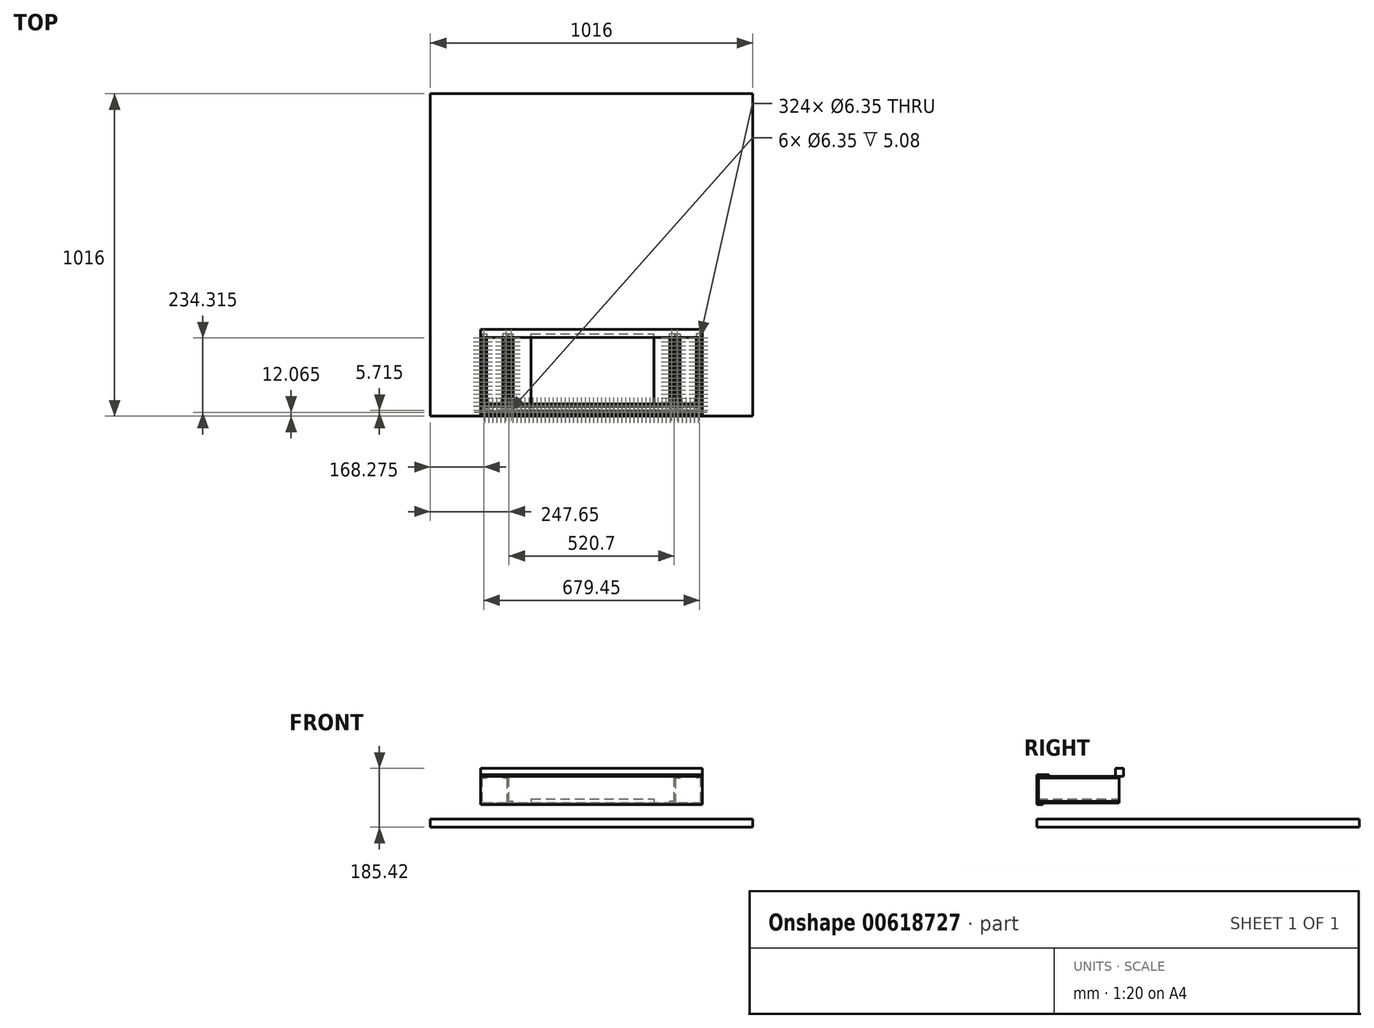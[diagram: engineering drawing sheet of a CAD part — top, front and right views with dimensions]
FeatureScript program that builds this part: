
annotation { "Feature Type Name" : "Feature", "Feature Type Description" : "" }
export const myFeature = defineFeature(function(context is Context, id is Id, definition is map)
    precondition{}
    {
        {
            var Q0;
            Q0=qCreatedBy(makeId("Top.planeOp"),FACE);
            var sketch = newSketch(context, id + "F0", { "sketchPlane" : qUnion([Q0])});
            skLineSegment(sketch, "E0.bottom", {"start": v(508, 508) * mm, "end": v(-508, 508) * mm});
            skLineSegment(sketch, "E0.top", {"start": v(508, -508) * mm, "end": v(-508, -508) * mm});
            skLineSegment(sketch, "E0.left", {"start": v(508, 508) * mm, "end": v(508, -508) * mm});
            skLineSegment(sketch, "E0.right", {"start": v(-508, 508) * mm, "end": v(-508, -508) * mm});
            skPoint(sketch, "E0.middle", {"position": v(0, 0) * mm});
            skSolve(sketch);
        }
        {
            var Q0;
            Q0 = qSketchRegion(id + "F0", true);
            extrude(context, id + "F1", {"entities" : qUnion([Q0]), "depth" : 25.4 * mm, "offsetDistance" : 25.4 * mm});
        }
        {
            var Q0;
            Q0=makeQuery(id+"F1.opExtrude","SWEPT_FACE",FACE,{"disambiguationData":[OSD([sQuery(id+"F0.wireOp",EDGE,"E0.top")])]});
            var sketch = newSketch(context, id + "F2", { "sketchPlane" : qUnion([Q0])});
            skLineSegment(sketch, "E1.bottom", {"start": v(-349.25, 165.1) * mm, "end": v(349.25, 165.1) * mm});
            skLineSegment(sketch, "E1.top", {"start": v(-349.25, 76.2) * mm, "end": v(349.25, 76.2) * mm});
            skLineSegment(sketch, "E1.left", {"start": v(-349.25, 165.1) * mm, "end": v(-349.25, 76.2) * mm});
            skLineSegment(sketch, "E1.right", {"start": v(349.25, 165.1) * mm, "end": v(349.25, 76.2) * mm});
            skSolve(sketch);
        }
        {
            var Q0;
            Q0 = qSketchRegion(id + "F2", true);
            extrude(context, id + "F3", {"entities" : qUnion([Q0]), "oppositeDirection" : true, "depth" : 5.08 * mm, "offsetDistance" : 25.4 * mm});
        }
        {
            var Q0;
            Q0=makeQuery(id+"F3.opExtrude","SWEPT_FACE",FACE,{"disambiguationData":[OSD([sQuery(id+"F2.wireOp",EDGE,"E1.bottom")])]});
            var sketch = newSketch(context, id + "F4", { "sketchPlane" : qUnion([Q0])});
            skLineSegment(sketch, "E2.bottom", {"start": v(-349.25, -469.9) * mm, "end": v(349.25, -469.9) * mm});
            skLineSegment(sketch, "E2.top", {"start": v(-349.25, -508) * mm, "end": v(349.25, -508) * mm});
            skLineSegment(sketch, "E2.left", {"start": v(-349.25, -469.9) * mm, "end": v(-349.25, -508) * mm});
            skLineSegment(sketch, "E2.right", {"start": v(349.25, -469.9) * mm, "end": v(349.25, -508) * mm});
            skCircle(sketch, "E3", {"center": v(-336.55, -476.25) * mm, "radius": 3.18 * mm});
            skCircle(sketch, "E4.0.1.0", {"center": v(-335.43, -495.27) * mm, "radius": 3.18 * mm});
            skCircle(sketch, "E4.1.0.0", {"center": v(-323.85, -476.25) * mm, "radius": 3.18 * mm});
            skCircle(sketch, "E4.1.1.0", {"center": v(-322.73, -495.27) * mm, "radius": 3.18 * mm});
            skCircle(sketch, "E4.2.0.0", {"center": v(-311.15, -476.25) * mm, "radius": 3.18 * mm});
            skCircle(sketch, "E4.2.1.0", {"center": v(-310.03, -495.27) * mm, "radius": 3.18 * mm});
            skCircle(sketch, "E4.3.0.0", {"center": v(-298.45, -476.25) * mm, "radius": 3.18 * mm});
            skCircle(sketch, "E4.3.1.0", {"center": v(-297.33, -495.27) * mm, "radius": 3.18 * mm});
            skCircle(sketch, "E4.4.0.0", {"center": v(-285.75, -476.25) * mm, "radius": 3.18 * mm});
            skCircle(sketch, "E4.4.1.0", {"center": v(-284.63, -495.27) * mm, "radius": 3.18 * mm});
            skCircle(sketch, "E4.5.0.0", {"center": v(-273.05, -476.25) * mm, "radius": 3.18 * mm});
            skCircle(sketch, "E4.5.1.0", {"center": v(-271.93, -495.27) * mm, "radius": 3.18 * mm});
            skCircle(sketch, "E4.6.0.0", {"center": v(-260.35, -476.25) * mm, "radius": 3.18 * mm});
            skCircle(sketch, "E4.6.1.0", {"center": v(-259.23, -495.27) * mm, "radius": 3.18 * mm});
            skCircle(sketch, "E4.7.0.0", {"center": v(-247.65, -476.25) * mm, "radius": 3.18 * mm});
            skCircle(sketch, "E4.7.1.0", {"center": v(-246.53, -495.27) * mm, "radius": 3.18 * mm});
            skCircle(sketch, "E4.8.0.0", {"center": v(-234.95, -476.25) * mm, "radius": 3.18 * mm});
            skCircle(sketch, "E4.8.1.0", {"center": v(-233.83, -495.27) * mm, "radius": 3.18 * mm});
            skCircle(sketch, "E4.9.0.0", {"center": v(-222.25, -476.25) * mm, "radius": 3.18 * mm});
            skCircle(sketch, "E4.9.1.0", {"center": v(-221.13, -495.27) * mm, "radius": 3.18 * mm});
            skCircle(sketch, "E4.10.0.0", {"center": v(-209.55, -476.25) * mm, "radius": 3.18 * mm});
            skCircle(sketch, "E4.10.1.0", {"center": v(-208.43, -495.27) * mm, "radius": 3.18 * mm});
            skCircle(sketch, "E4.11.0.0", {"center": v(-196.85, -476.25) * mm, "radius": 3.18 * mm});
            skCircle(sketch, "E4.11.1.0", {"center": v(-195.73, -495.27) * mm, "radius": 3.18 * mm});
            skCircle(sketch, "E4.12.0.0", {"center": v(-184.15, -476.25) * mm, "radius": 3.18 * mm});
            skCircle(sketch, "E4.12.1.0", {"center": v(-183.03, -495.27) * mm, "radius": 3.18 * mm});
            skCircle(sketch, "E4.13.0.0", {"center": v(-171.45, -476.25) * mm, "radius": 3.18 * mm});
            skCircle(sketch, "E4.13.1.0", {"center": v(-170.33, -495.27) * mm, "radius": 3.18 * mm});
            skCircle(sketch, "E4.14.0.0", {"center": v(-158.75, -476.25) * mm, "radius": 3.18 * mm});
            skCircle(sketch, "E4.14.1.0", {"center": v(-157.63, -495.27) * mm, "radius": 3.18 * mm});
            skCircle(sketch, "E4.15.0.0", {"center": v(-146.05, -476.25) * mm, "radius": 3.18 * mm});
            skCircle(sketch, "E4.15.1.0", {"center": v(-144.93, -495.27) * mm, "radius": 3.18 * mm});
            skCircle(sketch, "E4.16.0.0", {"center": v(-133.35, -476.25) * mm, "radius": 3.18 * mm});
            skCircle(sketch, "E4.16.1.0", {"center": v(-132.23, -495.27) * mm, "radius": 3.18 * mm});
            skCircle(sketch, "E4.17.0.0", {"center": v(-120.65, -476.25) * mm, "radius": 3.18 * mm});
            skCircle(sketch, "E4.17.1.0", {"center": v(-119.53, -495.27) * mm, "radius": 3.18 * mm});
            skCircle(sketch, "E4.18.0.0", {"center": v(-107.95, -476.25) * mm, "radius": 3.18 * mm});
            skCircle(sketch, "E4.18.1.0", {"center": v(-106.83, -495.27) * mm, "radius": 3.18 * mm});
            skCircle(sketch, "E4.19.0.0", {"center": v(-95.25, -476.25) * mm, "radius": 3.18 * mm});
            skCircle(sketch, "E4.19.1.0", {"center": v(-94.13, -495.27) * mm, "radius": 3.18 * mm});
            skCircle(sketch, "E4.20.0.0", {"center": v(-82.55, -476.25) * mm, "radius": 3.18 * mm});
            skCircle(sketch, "E4.20.1.0", {"center": v(-81.43, -495.27) * mm, "radius": 3.18 * mm});
            skCircle(sketch, "E4.21.0.0", {"center": v(-69.85, -476.25) * mm, "radius": 3.18 * mm});
            skCircle(sketch, "E4.21.1.0", {"center": v(-68.73, -495.27) * mm, "radius": 3.18 * mm});
            skCircle(sketch, "E4.22.0.0", {"center": v(-57.15, -476.25) * mm, "radius": 3.18 * mm});
            skCircle(sketch, "E4.22.1.0", {"center": v(-56.03, -495.27) * mm, "radius": 3.18 * mm});
            skCircle(sketch, "E4.23.0.0", {"center": v(-44.45, -476.25) * mm, "radius": 3.18 * mm});
            skCircle(sketch, "E4.23.1.0", {"center": v(-43.33, -495.27) * mm, "radius": 3.18 * mm});
            skCircle(sketch, "E4.24.0.0", {"center": v(-31.75, -476.25) * mm, "radius": 3.18 * mm});
            skCircle(sketch, "E4.24.1.0", {"center": v(-30.63, -495.27) * mm, "radius": 3.18 * mm});
            skCircle(sketch, "E4.25.0.0", {"center": v(-19.05, -476.25) * mm, "radius": 3.18 * mm});
            skCircle(sketch, "E4.25.1.0", {"center": v(-17.93, -495.27) * mm, "radius": 3.18 * mm});
            skCircle(sketch, "E4.26.0.0", {"center": v(-6.35, -476.25) * mm, "radius": 3.18 * mm});
            skCircle(sketch, "E4.26.1.0", {"center": v(-5.23, -495.27) * mm, "radius": 3.18 * mm});
            skCircle(sketch, "E4.27.0.0", {"center": v(6.35, -476.25) * mm, "radius": 3.18 * mm});
            skCircle(sketch, "E4.27.1.0", {"center": v(7.47, -495.27) * mm, "radius": 3.18 * mm});
            skCircle(sketch, "E4.28.0.0", {"center": v(19.05, -476.25) * mm, "radius": 3.18 * mm});
            skCircle(sketch, "E4.28.1.0", {"center": v(20.17, -495.27) * mm, "radius": 3.18 * mm});
            skCircle(sketch, "E4.29.0.0", {"center": v(31.75, -476.25) * mm, "radius": 3.18 * mm});
            skCircle(sketch, "E4.29.1.0", {"center": v(32.87, -495.27) * mm, "radius": 3.18 * mm});
            skCircle(sketch, "E4.30.0.0", {"center": v(44.45, -476.25) * mm, "radius": 3.18 * mm});
            skCircle(sketch, "E4.30.1.0", {"center": v(45.57, -495.27) * mm, "radius": 3.18 * mm});
            skCircle(sketch, "E4.31.0.0", {"center": v(57.15, -476.25) * mm, "radius": 3.18 * mm});
            skCircle(sketch, "E4.31.1.0", {"center": v(58.27, -495.27) * mm, "radius": 3.18 * mm});
            skCircle(sketch, "E4.32.0.0", {"center": v(69.85, -476.25) * mm, "radius": 3.18 * mm});
            skCircle(sketch, "E4.32.1.0", {"center": v(70.97, -495.27) * mm, "radius": 3.18 * mm});
            skCircle(sketch, "E4.33.0.0", {"center": v(82.55, -476.25) * mm, "radius": 3.18 * mm});
            skCircle(sketch, "E4.33.1.0", {"center": v(83.67, -495.27) * mm, "radius": 3.18 * mm});
            skCircle(sketch, "E4.34.0.0", {"center": v(95.25, -476.25) * mm, "radius": 3.18 * mm});
            skCircle(sketch, "E4.34.1.0", {"center": v(96.37, -495.27) * mm, "radius": 3.18 * mm});
            skCircle(sketch, "E4.35.0.0", {"center": v(107.95, -476.25) * mm, "radius": 3.18 * mm});
            skCircle(sketch, "E4.35.1.0", {"center": v(109.07, -495.27) * mm, "radius": 3.18 * mm});
            skCircle(sketch, "E4.36.0.0", {"center": v(120.65, -476.25) * mm, "radius": 3.18 * mm});
            skCircle(sketch, "E4.36.1.0", {"center": v(121.77, -495.27) * mm, "radius": 3.18 * mm});
            skCircle(sketch, "E4.37.0.0", {"center": v(133.35, -476.25) * mm, "radius": 3.18 * mm});
            skCircle(sketch, "E4.37.1.0", {"center": v(134.47, -495.27) * mm, "radius": 3.18 * mm});
            skCircle(sketch, "E4.38.0.0", {"center": v(146.05, -476.25) * mm, "radius": 3.18 * mm});
            skCircle(sketch, "E4.38.1.0", {"center": v(147.17, -495.27) * mm, "radius": 3.18 * mm});
            skCircle(sketch, "E4.39.0.0", {"center": v(158.75, -476.25) * mm, "radius": 3.18 * mm});
            skCircle(sketch, "E4.39.1.0", {"center": v(159.87, -495.27) * mm, "radius": 3.18 * mm});
            skCircle(sketch, "E4.40.0.0", {"center": v(171.45, -476.25) * mm, "radius": 3.18 * mm});
            skCircle(sketch, "E4.40.1.0", {"center": v(172.57, -495.27) * mm, "radius": 3.18 * mm});
            skCircle(sketch, "E4.41.0.0", {"center": v(184.15, -476.25) * mm, "radius": 3.18 * mm});
            skCircle(sketch, "E4.41.1.0", {"center": v(185.27, -495.27) * mm, "radius": 3.18 * mm});
            skCircle(sketch, "E4.42.0.0", {"center": v(196.85, -476.25) * mm, "radius": 3.18 * mm});
            skCircle(sketch, "E4.42.1.0", {"center": v(197.97, -495.27) * mm, "radius": 3.18 * mm});
            skCircle(sketch, "E4.43.0.0", {"center": v(209.55, -476.25) * mm, "radius": 3.18 * mm});
            skCircle(sketch, "E4.43.1.0", {"center": v(210.67, -495.27) * mm, "radius": 3.18 * mm});
            skCircle(sketch, "E4.44.0.0", {"center": v(222.25, -476.25) * mm, "radius": 3.18 * mm});
            skCircle(sketch, "E4.44.1.0", {"center": v(223.37, -495.27) * mm, "radius": 3.18 * mm});
            skCircle(sketch, "E4.45.0.0", {"center": v(234.95, -476.25) * mm, "radius": 3.18 * mm});
            skCircle(sketch, "E4.45.1.0", {"center": v(236.07, -495.27) * mm, "radius": 3.18 * mm});
            skCircle(sketch, "E4.46.0.0", {"center": v(247.65, -476.25) * mm, "radius": 3.18 * mm});
            skCircle(sketch, "E4.46.1.0", {"center": v(248.77, -495.27) * mm, "radius": 3.18 * mm});
            skCircle(sketch, "E4.47.0.0", {"center": v(260.35, -476.25) * mm, "radius": 3.18 * mm});
            skCircle(sketch, "E4.47.1.0", {"center": v(261.47, -495.27) * mm, "radius": 3.18 * mm});
            skCircle(sketch, "E4.48.0.0", {"center": v(273.05, -476.25) * mm, "radius": 3.18 * mm});
            skCircle(sketch, "E4.48.1.0", {"center": v(274.17, -495.27) * mm, "radius": 3.18 * mm});
            skCircle(sketch, "E4.49.0.0", {"center": v(285.75, -476.25) * mm, "radius": 3.18 * mm});
            skCircle(sketch, "E4.49.1.0", {"center": v(286.87, -495.27) * mm, "radius": 3.18 * mm});
            skCircle(sketch, "E4.50.0.0", {"center": v(298.45, -476.25) * mm, "radius": 3.18 * mm});
            skCircle(sketch, "E4.50.1.0", {"center": v(299.57, -495.27) * mm, "radius": 3.18 * mm});
            skCircle(sketch, "E4.51.0.0", {"center": v(311.15, -476.25) * mm, "radius": 3.18 * mm});
            skCircle(sketch, "E4.51.1.0", {"center": v(312.27, -495.27) * mm, "radius": 3.18 * mm});
            skCircle(sketch, "E4.52.0.0", {"center": v(323.85, -476.25) * mm, "radius": 3.18 * mm});
            skCircle(sketch, "E4.52.1.0", {"center": v(324.97, -495.27) * mm, "radius": 3.18 * mm});
            skCircle(sketch, "E4.53.0.0", {"center": v(336.55, -476.25) * mm, "radius": 3.18 * mm});
            skCircle(sketch, "E4.53.1.0", {"center": v(337.67, -495.27) * mm, "radius": 3.18 * mm});
            skLineSegment(sketch, "E4.direction1", {"start": v(-336.55, -476.25) * mm, "end": v(-323.85, -476.25) * mm, "construction": true});
            skLineSegment(sketch, "E4.direction2", {"start": v(-336.55, -476.25) * mm, "end": v(-335.43, -495.27) * mm, "construction": true});
            skSolve(sketch);
        }
        {
            var Q0;
            Q0 = qSketchRegion(id + "F4", true);
            extrude(context, id + "F5", {"entities" : qUnion([Q0]), "oppositeDirection" : true, "depth" : 5.08 * mm, "offsetDistance" : 25.4 * mm});
        }
        {
            var Q0;
            Q0=makeQuery(id+"F3.opExtrude","SWEPT_FACE",FACE,{"disambiguationData":[OSD([sQuery(id+"F2.wireOp",EDGE,"E1.top")])]});
            var sketch = newSketch(context, id + "F6", { "sketchPlane" : qUnion([Q0])});
            skLineSegment(sketch, "E5.bottom", {"start": v(-349.25, 508) * mm, "end": v(349.25, 508) * mm});
            skLineSegment(sketch, "E5.top", {"start": v(-349.25, 488.95) * mm, "end": v(349.25, 488.95) * mm});
            skLineSegment(sketch, "E5.left", {"start": v(-349.25, 508) * mm, "end": v(-349.25, 488.95) * mm});
            skLineSegment(sketch, "E5.right", {"start": v(349.25, 508) * mm, "end": v(349.25, 488.95) * mm});
            skCircle(sketch, "E6", {"center": v(-336.55, 495.94) * mm, "radius": 3.18 * mm});
            skCircle(sketch, "E7.1.0.0", {"center": v(-323.85, 495.94) * mm, "radius": 3.18 * mm});
            skCircle(sketch, "E7.2.0.0", {"center": v(-311.15, 495.94) * mm, "radius": 3.18 * mm});
            skCircle(sketch, "E7.3.0.0", {"center": v(-298.45, 495.94) * mm, "radius": 3.18 * mm});
            skCircle(sketch, "E7.4.0.0", {"center": v(-285.75, 495.94) * mm, "radius": 3.18 * mm});
            skCircle(sketch, "E7.5.0.0", {"center": v(-273.05, 495.94) * mm, "radius": 3.18 * mm});
            skCircle(sketch, "E7.6.0.0", {"center": v(-260.35, 495.94) * mm, "radius": 3.18 * mm});
            skCircle(sketch, "E7.7.0.0", {"center": v(-247.65, 495.94) * mm, "radius": 3.18 * mm});
            skCircle(sketch, "E7.8.0.0", {"center": v(-234.95, 495.94) * mm, "radius": 3.18 * mm});
            skCircle(sketch, "E7.9.0.0", {"center": v(-222.25, 495.94) * mm, "radius": 3.18 * mm});
            skCircle(sketch, "E7.10.0.0", {"center": v(-209.55, 495.94) * mm, "radius": 3.18 * mm});
            skCircle(sketch, "E7.11.0.0", {"center": v(-196.85, 495.94) * mm, "radius": 3.18 * mm});
            skCircle(sketch, "E7.12.0.0", {"center": v(-184.15, 495.94) * mm, "radius": 3.18 * mm});
            skCircle(sketch, "E7.13.0.0", {"center": v(-171.45, 495.94) * mm, "radius": 3.18 * mm});
            skCircle(sketch, "E7.14.0.0", {"center": v(-158.75, 495.94) * mm, "radius": 3.18 * mm});
            skCircle(sketch, "E7.15.0.0", {"center": v(-146.05, 495.94) * mm, "radius": 3.18 * mm});
            skCircle(sketch, "E7.16.0.0", {"center": v(-133.35, 495.94) * mm, "radius": 3.18 * mm});
            skCircle(sketch, "E7.17.0.0", {"center": v(-120.65, 495.94) * mm, "radius": 3.18 * mm});
            skCircle(sketch, "E7.18.0.0", {"center": v(-107.95, 495.94) * mm, "radius": 3.18 * mm});
            skCircle(sketch, "E7.19.0.0", {"center": v(-95.25, 495.94) * mm, "radius": 3.18 * mm});
            skCircle(sketch, "E7.20.0.0", {"center": v(-82.55, 495.94) * mm, "radius": 3.18 * mm});
            skCircle(sketch, "E7.21.0.0", {"center": v(-69.85, 495.94) * mm, "radius": 3.18 * mm});
            skCircle(sketch, "E7.22.0.0", {"center": v(-57.15, 495.94) * mm, "radius": 3.18 * mm});
            skCircle(sketch, "E7.23.0.0", {"center": v(-44.45, 495.94) * mm, "radius": 3.18 * mm});
            skCircle(sketch, "E7.24.0.0", {"center": v(-31.75, 495.94) * mm, "radius": 3.18 * mm});
            skCircle(sketch, "E7.25.0.0", {"center": v(-19.05, 495.94) * mm, "radius": 3.18 * mm});
            skCircle(sketch, "E7.26.0.0", {"center": v(-6.35, 495.94) * mm, "radius": 3.18 * mm});
            skCircle(sketch, "E7.27.0.0", {"center": v(6.35, 495.94) * mm, "radius": 3.18 * mm});
            skCircle(sketch, "E7.28.0.0", {"center": v(19.05, 495.94) * mm, "radius": 3.18 * mm});
            skCircle(sketch, "E7.29.0.0", {"center": v(31.75, 495.94) * mm, "radius": 3.18 * mm});
            skCircle(sketch, "E7.30.0.0", {"center": v(44.45, 495.94) * mm, "radius": 3.18 * mm});
            skCircle(sketch, "E7.31.0.0", {"center": v(57.15, 495.94) * mm, "radius": 3.18 * mm});
            skCircle(sketch, "E7.32.0.0", {"center": v(69.85, 495.94) * mm, "radius": 3.18 * mm});
            skCircle(sketch, "E7.33.0.0", {"center": v(82.55, 495.94) * mm, "radius": 3.18 * mm});
            skCircle(sketch, "E7.34.0.0", {"center": v(95.25, 495.94) * mm, "radius": 3.18 * mm});
            skCircle(sketch, "E7.35.0.0", {"center": v(107.95, 495.94) * mm, "radius": 3.18 * mm});
            skCircle(sketch, "E7.36.0.0", {"center": v(120.65, 495.94) * mm, "radius": 3.18 * mm});
            skCircle(sketch, "E7.37.0.0", {"center": v(133.35, 495.94) * mm, "radius": 3.18 * mm});
            skCircle(sketch, "E7.38.0.0", {"center": v(146.05, 495.94) * mm, "radius": 3.18 * mm});
            skCircle(sketch, "E7.39.0.0", {"center": v(158.75, 495.94) * mm, "radius": 3.18 * mm});
            skCircle(sketch, "E7.40.0.0", {"center": v(171.45, 495.94) * mm, "radius": 3.18 * mm});
            skCircle(sketch, "E7.41.0.0", {"center": v(184.15, 495.94) * mm, "radius": 3.18 * mm});
            skCircle(sketch, "E7.42.0.0", {"center": v(196.85, 495.94) * mm, "radius": 3.18 * mm});
            skCircle(sketch, "E7.43.0.0", {"center": v(209.55, 495.94) * mm, "radius": 3.18 * mm});
            skCircle(sketch, "E7.44.0.0", {"center": v(222.25, 495.94) * mm, "radius": 3.18 * mm});
            skCircle(sketch, "E7.45.0.0", {"center": v(234.95, 495.94) * mm, "radius": 3.18 * mm});
            skCircle(sketch, "E7.46.0.0", {"center": v(247.65, 495.94) * mm, "radius": 3.18 * mm});
            skCircle(sketch, "E7.47.0.0", {"center": v(260.35, 495.94) * mm, "radius": 3.18 * mm});
            skCircle(sketch, "E7.48.0.0", {"center": v(273.05, 495.94) * mm, "radius": 3.18 * mm});
            skCircle(sketch, "E7.49.0.0", {"center": v(285.75, 495.94) * mm, "radius": 3.18 * mm});
            skCircle(sketch, "E7.50.0.0", {"center": v(298.45, 495.94) * mm, "radius": 3.18 * mm});
            skCircle(sketch, "E7.51.0.0", {"center": v(311.15, 495.94) * mm, "radius": 3.18 * mm});
            skCircle(sketch, "E7.52.0.0", {"center": v(323.85, 495.94) * mm, "radius": 3.18 * mm});
            skCircle(sketch, "E7.53.0.0", {"center": v(336.55, 495.94) * mm, "radius": 3.18 * mm});
            skLineSegment(sketch, "E7.direction1", {"start": v(-336.55, 495.94) * mm, "end": v(-323.85, 495.94) * mm, "construction": true});
            skSolve(sketch);
        }
        {
            var Q0;
            Q0 = qSketchRegion(id + "F6", true);
            extrude(context, id + "F7", {"entities" : qUnion([Q0]), "operationType" : NewBodyOperationType.ADD, "depth" : 5.08 * mm, "offsetDistance" : 25.4 * mm});
        }
        {
            var Q0;
            Q0=makeQuery(id+"F3.opExtrude","CAP_FACE",FACE,{"disambiguationData":[OSD([sQuery(id+"F2.wireOp",EDGE,"E1.bottom"),sQuery(id+"F2.wireOp",EDGE,"E1.top"),sQuery(id+"F2.wireOp",EDGE,"E1.left"),sQuery(id+"F2.wireOp",EDGE,"E1.right")])],"isStart":false});
            var sketch = newSketch(context, id + "F8", { "sketchPlane" : qUnion([Q0])});
            skLineSegment(sketch, "E8.top", {"start": v(-349.25, 154.94) * mm, "end": v(-344.17, 154.94) * mm});
            skLineSegment(sketch, "E8.left", {"start": v(-349.25, 81.28) * mm, "end": v(-349.25, 154.94) * mm});
            skLineSegment(sketch, "E8.right", {"start": v(-344.17, 81.28) * mm, "end": v(-344.17, 154.94) * mm});
            skLineSegment(sketch, "E9.top", {"start": v(-265.43, 154.94) * mm, "end": v(-260.35, 154.94) * mm});
            skLineSegment(sketch, "E9.left", {"start": v(-265.43, 81.28) * mm, "end": v(-265.43, 154.94) * mm});
            skLineSegment(sketch, "E9.right", {"start": v(-260.35, 81.28) * mm, "end": v(-260.35, 154.94) * mm});
            skLineSegment(sketch, "E10", {"start": v(-265.43, 81.28) * mm, "end": v(-260.35, 81.28) * mm});
            skLineSegment(sketch, "E11", {"start": v(-349.25, 81.28) * mm, "end": v(-344.17, 81.28) * mm});
            skSolve(sketch);
        }
        {
            var Q0;
            Q0 = qSketchRegion(id + "F8", true);
            extrude(context, id + "F9", {"entities" : qUnion([Q0]), "operationType" : NewBodyOperationType.ADD, "depth" : 254 * mm, "offsetDistance" : 25.4 * mm});
        }
        {
            var Q0;
            Q0=makeQuery(id+"F9.opExtrude","SWEPT_FACE",FACE,{"disambiguationData":[OSD([sQuery(id+"F8.wireOp",EDGE,"E8.top")])]});
            var sketch = newSketch(context, id + "F10", { "sketchPlane" : qUnion([Q0])});
            skLineSegment(sketch, "E12.bottom", {"start": v(349.25, -248.92) * mm, "end": v(330.2, -248.92) * mm});
            skLineSegment(sketch, "E12.top", {"start": v(349.25, -502.92) * mm, "end": v(330.2, -502.92) * mm});
            skLineSegment(sketch, "E12.left", {"start": v(349.25, -248.92) * mm, "end": v(349.25, -502.92) * mm});
            skLineSegment(sketch, "E12.right", {"start": v(330.2, -248.92) * mm, "end": v(330.2, -502.92) * mm});
            skLineSegment(sketch, "E13.bottom", {"start": v(260.35, -248.92) * mm, "end": v(279.4, -248.92) * mm});
            skLineSegment(sketch, "E13.top", {"start": v(260.35, -502.92) * mm, "end": v(279.4, -502.92) * mm});
            skLineSegment(sketch, "E13.left", {"start": v(260.35, -248.92) * mm, "end": v(260.35, -502.92) * mm});
            skLineSegment(sketch, "E13.right", {"start": v(279.4, -248.92) * mm, "end": v(279.4, -502.92) * mm});
            skCircle(sketch, "E14", {"center": v(269.88, -261.62) * mm, "radius": 3.18 * mm});
            skCircle(sketch, "E15.0.1.0", {"center": v(269.88, -274.32) * mm, "radius": 3.18 * mm});
            skCircle(sketch, "E15.0.2.0", {"center": v(269.88, -287.02) * mm, "radius": 3.18 * mm});
            skCircle(sketch, "E15.0.3.0", {"center": v(269.88, -299.72) * mm, "radius": 3.18 * mm});
            skCircle(sketch, "E15.0.4.0", {"center": v(269.88, -312.42) * mm, "radius": 3.18 * mm});
            skCircle(sketch, "E15.0.5.0", {"center": v(269.88, -325.12) * mm, "radius": 3.18 * mm});
            skCircle(sketch, "E15.0.6.0", {"center": v(269.88, -337.82) * mm, "radius": 3.18 * mm});
            skCircle(sketch, "E15.0.7.0", {"center": v(269.88, -350.52) * mm, "radius": 3.18 * mm});
            skCircle(sketch, "E15.0.8.0", {"center": v(269.88, -363.22) * mm, "radius": 3.18 * mm});
            skCircle(sketch, "E15.0.9.0", {"center": v(269.88, -375.92) * mm, "radius": 3.18 * mm});
            skCircle(sketch, "E15.0.10.0", {"center": v(269.88, -388.62) * mm, "radius": 3.18 * mm});
            skCircle(sketch, "E15.0.11.0", {"center": v(269.88, -401.32) * mm, "radius": 3.18 * mm});
            skCircle(sketch, "E15.0.12.0", {"center": v(269.88, -414.02) * mm, "radius": 3.18 * mm});
            skCircle(sketch, "E15.0.13.0", {"center": v(269.88, -426.72) * mm, "radius": 3.18 * mm});
            skCircle(sketch, "E15.0.14.0", {"center": v(269.88, -439.42) * mm, "radius": 3.18 * mm});
            skCircle(sketch, "E15.0.15.0", {"center": v(269.88, -452.12) * mm, "radius": 3.18 * mm});
            skCircle(sketch, "E15.0.16.0", {"center": v(269.88, -464.82) * mm, "radius": 3.18 * mm});
            skCircle(sketch, "E15.0.17.0", {"center": v(269.88, -477.52) * mm, "radius": 3.18 * mm});
            skCircle(sketch, "E15.0.18.0", {"center": v(269.88, -490.22) * mm, "radius": 3.18 * mm});
            skCircle(sketch, "E15.1.0.0", {"center": v(339.73, -261.62) * mm, "radius": 3.18 * mm});
            skCircle(sketch, "E15.1.1.0", {"center": v(339.73, -274.32) * mm, "radius": 3.18 * mm});
            skCircle(sketch, "E15.1.2.0", {"center": v(339.73, -287.02) * mm, "radius": 3.18 * mm});
            skCircle(sketch, "E15.1.3.0", {"center": v(339.73, -299.72) * mm, "radius": 3.18 * mm});
            skCircle(sketch, "E15.1.4.0", {"center": v(339.73, -312.42) * mm, "radius": 3.18 * mm});
            skCircle(sketch, "E15.1.5.0", {"center": v(339.73, -325.12) * mm, "radius": 3.18 * mm});
            skCircle(sketch, "E15.1.6.0", {"center": v(339.73, -337.82) * mm, "radius": 3.18 * mm});
            skCircle(sketch, "E15.1.7.0", {"center": v(339.73, -350.52) * mm, "radius": 3.18 * mm});
            skCircle(sketch, "E15.1.8.0", {"center": v(339.73, -363.22) * mm, "radius": 3.18 * mm});
            skCircle(sketch, "E15.1.9.0", {"center": v(339.73, -375.92) * mm, "radius": 3.18 * mm});
            skCircle(sketch, "E15.1.10.0", {"center": v(339.73, -388.62) * mm, "radius": 3.18 * mm});
            skCircle(sketch, "E15.1.11.0", {"center": v(339.73, -401.32) * mm, "radius": 3.18 * mm});
            skCircle(sketch, "E15.1.12.0", {"center": v(339.73, -414.02) * mm, "radius": 3.18 * mm});
            skCircle(sketch, "E15.1.13.0", {"center": v(339.73, -426.72) * mm, "radius": 3.18 * mm});
            skCircle(sketch, "E15.1.14.0", {"center": v(339.73, -439.42) * mm, "radius": 3.18 * mm});
            skCircle(sketch, "E15.1.15.0", {"center": v(339.73, -452.12) * mm, "radius": 3.18 * mm});
            skCircle(sketch, "E15.1.16.0", {"center": v(339.73, -464.82) * mm, "radius": 3.18 * mm});
            skCircle(sketch, "E15.1.17.0", {"center": v(339.73, -477.52) * mm, "radius": 3.18 * mm});
            skCircle(sketch, "E15.1.18.0", {"center": v(339.73, -490.22) * mm, "radius": 3.18 * mm});
            skLineSegment(sketch, "E15.direction1", {"start": v(269.88, -261.62) * mm, "end": v(339.73, -261.62) * mm, "construction": true});
            skLineSegment(sketch, "E15.direction2", {"start": v(269.88, -261.62) * mm, "end": v(269.88, -274.32) * mm, "construction": true});
            skSolve(sketch);
        }
        {
            var Q0;
            Q0 = qSketchRegion(id + "F10", true);
            extrude(context, id + "F11", {"entities" : qUnion([Q0]), "depth" : 5.08 * mm, "offsetDistance" : 25.4 * mm});
        }
        {
            var Q0;
            Q0=makeQuery(id+"F9.opExtrude","SWEPT_FACE",FACE,{"disambiguationData":[OSD([sQuery(id+"F8.wireOp",EDGE,"E10")])]});
            var sketch = newSketch(context, id + "F12", { "sketchPlane" : qUnion([Q0])});
            skLineSegment(sketch, "E16.bottom", {"start": v(246.38, 502.92) * mm, "end": v(265.43, 502.92) * mm});
            skLineSegment(sketch, "E16.top", {"start": v(246.38, 248.92) * mm, "end": v(265.43, 248.92) * mm});
            skLineSegment(sketch, "E16.left", {"start": v(246.38, 502.92) * mm, "end": v(246.38, 248.92) * mm});
            skLineSegment(sketch, "E16.right", {"start": v(265.43, 502.92) * mm, "end": v(265.43, 248.92) * mm});
            skCircle(sketch, "E17", {"center": v(252.73, 261.62) * mm, "radius": 3.18 * mm});
            skCircle(sketch, "E18.0.1.0", {"center": v(252.73, 274.32) * mm, "radius": 3.18 * mm});
            skCircle(sketch, "E18.0.2.0", {"center": v(252.73, 287.02) * mm, "radius": 3.18 * mm});
            skCircle(sketch, "E18.0.3.0", {"center": v(252.73, 299.72) * mm, "radius": 3.18 * mm});
            skCircle(sketch, "E18.0.4.0", {"center": v(252.73, 312.42) * mm, "radius": 3.18 * mm});
            skCircle(sketch, "E18.0.5.0", {"center": v(252.73, 325.12) * mm, "radius": 3.18 * mm});
            skCircle(sketch, "E18.0.6.0", {"center": v(252.73, 337.82) * mm, "radius": 3.18 * mm});
            skCircle(sketch, "E18.0.7.0", {"center": v(252.73, 350.52) * mm, "radius": 3.18 * mm});
            skCircle(sketch, "E18.0.8.0", {"center": v(252.73, 363.22) * mm, "radius": 3.18 * mm});
            skCircle(sketch, "E18.0.9.0", {"center": v(252.73, 375.92) * mm, "radius": 3.18 * mm});
            skCircle(sketch, "E18.0.10.0", {"center": v(252.73, 388.62) * mm, "radius": 3.18 * mm});
            skCircle(sketch, "E18.0.11.0", {"center": v(252.73, 401.32) * mm, "radius": 3.18 * mm});
            skCircle(sketch, "E18.0.12.0", {"center": v(252.73, 414.02) * mm, "radius": 3.18 * mm});
            skCircle(sketch, "E18.0.13.0", {"center": v(252.73, 426.72) * mm, "radius": 3.18 * mm});
            skCircle(sketch, "E18.0.14.0", {"center": v(252.73, 439.42) * mm, "radius": 3.18 * mm});
            skCircle(sketch, "E18.0.15.0", {"center": v(252.73, 452.12) * mm, "radius": 3.18 * mm});
            skCircle(sketch, "E18.0.16.0", {"center": v(252.73, 464.82) * mm, "radius": 3.18 * mm});
            skCircle(sketch, "E18.0.17.0", {"center": v(252.73, 477.52) * mm, "radius": 3.18 * mm});
            skCircle(sketch, "E18.0.18.0", {"center": v(252.73, 490.22) * mm, "radius": 3.18 * mm});
            skLineSegment(sketch, "E18.direction1", {"start": v(252.73, 261.62) * mm, "end": v(278.13, 261.62) * mm, "construction": true});
            skLineSegment(sketch, "E18.direction2", {"start": v(252.73, 261.62) * mm, "end": v(252.73, 274.32) * mm, "construction": true});
            skSolve(sketch);
        }
        {
            var Q0;
            Q0 = qSketchRegion(id + "F12", true);
            extrude(context, id + "F13", {"entities" : qUnion([Q0]), "operationType" : NewBodyOperationType.ADD, "depth" : 5.08 * mm, "offsetDistance" : 25.4 * mm});
        }
        {
            var Q0;
            Q0=makeQuery(id+"F3.opExtrude","SWEPT_BODY",BODY,{"disambiguationData":[OSD([sQuery(id+"F2.wireOp",EDGE,"E1.bottom"),sQuery(id+"F2.wireOp",EDGE,"E1.top"),sQuery(id+"F2.wireOp",EDGE,"E1.left"),sQuery(id+"F2.wireOp",EDGE,"E1.right")])]});
            var Q1;
            Q1=makeQuery(id+"F11.opExtrude","SWEPT_BODY",BODY,{"disambiguationData":[OSD([sQuery(id+"F10.wireOp",EDGE,"E13.bottom"),sQuery(id+"F10.wireOp",EDGE,"E13.top"),sQuery(id+"F10.wireOp",EDGE,"E13.left"),sQuery(id+"F10.wireOp",EDGE,"E13.right"),sQuery(id+"F10.wireOp",EDGE,"E14"),sQuery(id+"F10.wireOp",EDGE,"E15.0.1.0"),sQuery(id+"F10.wireOp",EDGE,"E15.0.2.0"),sQuery(id+"F10.wireOp",EDGE,"E15.0.3.0"),sQuery(id+"F10.wireOp",EDGE,"E15.0.4.0"),sQuery(id+"F10.wireOp",EDGE,"E15.0.5.0"),sQuery(id+"F10.wireOp",EDGE,"E15.0.6.0"),sQuery(id+"F10.wireOp",EDGE,"E15.0.7.0"),sQuery(id+"F10.wireOp",EDGE,"E15.0.8.0"),sQuery(id+"F10.wireOp",EDGE,"E15.0.9.0"),sQuery(id+"F10.wireOp",EDGE,"E15.0.10.0"),sQuery(id+"F10.wireOp",EDGE,"E15.0.11.0"),sQuery(id+"F10.wireOp",EDGE,"E15.0.12.0"),sQuery(id+"F10.wireOp",EDGE,"E15.0.13.0"),sQuery(id+"F10.wireOp",EDGE,"E15.0.14.0"),sQuery(id+"F10.wireOp",EDGE,"E15.0.15.0"),sQuery(id+"F10.wireOp",EDGE,"E15.0.16.0"),sQuery(id+"F10.wireOp",EDGE,"E15.0.17.0"),sQuery(id+"F10.wireOp",EDGE,"E15.0.18.0")])]});
            var Q2;
            Q2=makeQuery(id+"F11.opExtrude","SWEPT_BODY",BODY,{"disambiguationData":[OSD([sQuery(id+"F10.wireOp",EDGE,"E12.bottom"),sQuery(id+"F10.wireOp",EDGE,"E12.top"),sQuery(id+"F10.wireOp",EDGE,"E12.left"),sQuery(id+"F10.wireOp",EDGE,"E12.right"),sQuery(id+"F10.wireOp",EDGE,"E15.1.0.0"),sQuery(id+"F10.wireOp",EDGE,"E15.1.1.0"),sQuery(id+"F10.wireOp",EDGE,"E15.1.2.0"),sQuery(id+"F10.wireOp",EDGE,"E15.1.3.0"),sQuery(id+"F10.wireOp",EDGE,"E15.1.4.0"),sQuery(id+"F10.wireOp",EDGE,"E15.1.5.0"),sQuery(id+"F10.wireOp",EDGE,"E15.1.6.0"),sQuery(id+"F10.wireOp",EDGE,"E15.1.7.0"),sQuery(id+"F10.wireOp",EDGE,"E15.1.8.0"),sQuery(id+"F10.wireOp",EDGE,"E15.1.9.0"),sQuery(id+"F10.wireOp",EDGE,"E15.1.10.0"),sQuery(id+"F10.wireOp",EDGE,"E15.1.11.0"),sQuery(id+"F10.wireOp",EDGE,"E15.1.12.0"),sQuery(id+"F10.wireOp",EDGE,"E15.1.13.0"),sQuery(id+"F10.wireOp",EDGE,"E15.1.14.0"),sQuery(id+"F10.wireOp",EDGE,"E15.1.15.0"),sQuery(id+"F10.wireOp",EDGE,"E15.1.16.0"),sQuery(id+"F10.wireOp",EDGE,"E15.1.17.0"),sQuery(id+"F10.wireOp",EDGE,"E15.1.18.0")])]});
            var Q3;
            Q3=qCreatedBy(makeId("Right.planeOp"),FACE);
            mirror(context, id + "F14", {"entities" : qUnion([Q0, Q1, Q2]), "mirrorPlane" : qUnion([Q3])});
        }
        {
            var Q0;
            Q0=makeQuery(id+"F14.opPattern","COPY",FACE,{"derivedFrom":makeQuery(id+"F11.opExtrude","CAP_FACE",FACE,{"disambiguationData":[OSD([sQuery(id+"F10.wireOp",EDGE,"E12.bottom"),sQuery(id+"F10.wireOp",EDGE,"E12.top"),sQuery(id+"F10.wireOp",EDGE,"E12.left"),sQuery(id+"F10.wireOp",EDGE,"E12.right"),sQuery(id+"F10.wireOp",EDGE,"E15.1.0.0"),sQuery(id+"F10.wireOp",EDGE,"E15.1.1.0"),sQuery(id+"F10.wireOp",EDGE,"E15.1.2.0"),sQuery(id+"F10.wireOp",EDGE,"E15.1.3.0"),sQuery(id+"F10.wireOp",EDGE,"E15.1.4.0"),sQuery(id+"F10.wireOp",EDGE,"E15.1.5.0"),sQuery(id+"F10.wireOp",EDGE,"E15.1.6.0"),sQuery(id+"F10.wireOp",EDGE,"E15.1.7.0"),sQuery(id+"F10.wireOp",EDGE,"E15.1.8.0"),sQuery(id+"F10.wireOp",EDGE,"E15.1.9.0"),sQuery(id+"F10.wireOp",EDGE,"E15.1.10.0"),sQuery(id+"F10.wireOp",EDGE,"E15.1.11.0"),sQuery(id+"F10.wireOp",EDGE,"E15.1.12.0"),sQuery(id+"F10.wireOp",EDGE,"E15.1.13.0"),sQuery(id+"F10.wireOp",EDGE,"E15.1.14.0"),sQuery(id+"F10.wireOp",EDGE,"E15.1.15.0"),sQuery(id+"F10.wireOp",EDGE,"E15.1.16.0"),sQuery(id+"F10.wireOp",EDGE,"E15.1.17.0"),sQuery(id+"F10.wireOp",EDGE,"E15.1.18.0")])],"isStart":false}),"instanceName":"1"});
            var sketch = newSketch(context, id + "F15", { "sketchPlane" : qUnion([Q0])});
            skLineSegment(sketch, "E19.bottom", {"start": v(-349.25, -234.95) * mm, "end": v(349.25, -234.95) * mm});
            skLineSegment(sketch, "E19.top", {"start": v(-349.25, -260.35) * mm, "end": v(349.25, -260.35) * mm});
            skLineSegment(sketch, "E19.left", {"start": v(-349.25, -234.95) * mm, "end": v(-349.25, -260.35) * mm});
            skLineSegment(sketch, "E19.right", {"start": v(349.25, -234.95) * mm, "end": v(349.25, -260.35) * mm});
            skSolve(sketch);
        }
        {
            var Q0;
            Q0 = qSketchRegion(id + "F15", true);
            extrude(context, id + "F16", {"entities" : qUnion([Q0]), "depth" : 25.4 * mm, "offsetDistance" : 25.4 * mm});
        }
        {
            var Q0;
            {var subQ0=sQuery(id+"F6.wireOp",EDGE,"E7.41.0.0");var subQ1=sQuery(id+"F6.wireOp",EDGE,"E7.40.0.0");var subQ2=sQuery(id+"F6.wireOp",EDGE,"E7.39.0.0");var subQ3=sQuery(id+"F6.wireOp",EDGE,"E7.38.0.0");var subQ4=sQuery(id+"F6.wireOp",EDGE,"E7.37.0.0");var subQ5=sQuery(id+"F6.wireOp",EDGE,"E7.35.0.0");var subQ6=sQuery(id+"F6.wireOp",EDGE,"E7.33.0.0");var subQ7=sQuery(id+"F6.wireOp",EDGE,"E7.32.0.0");var subQ8=sQuery(id+"F6.wireOp",EDGE,"E7.31.0.0");var subQ9=sQuery(id+"F6.wireOp",EDGE,"E7.30.0.0");var subQ10=sQuery(id+"F6.wireOp",EDGE,"E7.29.0.0");var subQ11=sQuery(id+"F6.wireOp",EDGE,"E7.28.0.0");var subQ12=sQuery(id+"F6.wireOp",EDGE,"E7.27.0.0");var subQ13=sQuery(id+"F6.wireOp",EDGE,"E7.26.0.0");var subQ14=sQuery(id+"F6.wireOp",EDGE,"E7.25.0.0");var subQ15=sQuery(id+"F6.wireOp",EDGE,"E7.24.0.0");var subQ16=sQuery(id+"F6.wireOp",EDGE,"E7.23.0.0");var subQ17=sQuery(id+"F6.wireOp",EDGE,"E7.22.0.0");var subQ18=sQuery(id+"F6.wireOp",EDGE,"E7.21.0.0");var subQ19=sQuery(id+"F6.wireOp",EDGE,"E7.20.0.0");var subQ20=sQuery(id+"F6.wireOp",EDGE,"E7.19.0.0");var subQ21=sQuery(id+"F6.wireOp",EDGE,"E7.18.0.0");var subQ22=sQuery(id+"F6.wireOp",EDGE,"E7.4.0.0");var subQ23=sQuery(id+"F6.wireOp",EDGE,"E7.3.0.0");var subQ24=sQuery(id+"F6.wireOp",EDGE,"E7.2.0.0");var subQ25=sQuery(id+"F6.wireOp",EDGE,"E7.1.0.0");var subQ26=sQuery(id+"F6.wireOp",EDGE,"E6");var subQ27=sQuery(id+"F6.wireOp",EDGE,"E7.5.0.0");var subQ28=sQuery(id+"F6.wireOp",EDGE,"E7.34.0.0");var subQ29=sQuery(id+"F2.wireOp",EDGE,"E1.left");var subQ30=sQuery(id+"F6.wireOp",EDGE,"E7.11.0.0");var subQ31=sQuery(id+"F6.wireOp",EDGE,"E7.36.0.0");var subQ32=sQuery(id+"F6.wireOp",EDGE,"E7.13.0.0");var subQ33=sQuery(id+"F6.wireOp",EDGE,"E5.top");var subQ34=sQuery(id+"F6.wireOp",EDGE,"E5.left");var subQ35=sQuery(id+"F6.wireOp",EDGE,"E7.6.0.0");var subQ36=sQuery(id+"F6.wireOp",EDGE,"E7.7.0.0");var subQ37=sQuery(id+"F6.wireOp",EDGE,"E7.8.0.0");var subQ38=sQuery(id+"F6.wireOp",EDGE,"E7.9.0.0");var subQ39=sQuery(id+"F6.wireOp",EDGE,"E7.10.0.0");var subQ40=sQuery(id+"F6.wireOp",EDGE,"E7.12.0.0");var subQ41=sQuery(id+"F6.wireOp",EDGE,"E7.14.0.0");var subQ42=sQuery(id+"F6.wireOp",EDGE,"E7.15.0.0");var subQ43=sQuery(id+"F6.wireOp",EDGE,"E7.16.0.0");var subQ44=sQuery(id+"F6.wireOp",EDGE,"E7.17.0.0");var subQ45=sQuery(id+"F6.wireOp",EDGE,"E7.42.0.0");var subQ46=sQuery(id+"F6.wireOp",EDGE,"E7.43.0.0");var subQ47=sQuery(id+"F6.wireOp",EDGE,"E7.44.0.0");var subQ48=sQuery(id+"F6.wireOp",EDGE,"E7.45.0.0");var subQ49=sQuery(id+"F6.wireOp",EDGE,"E7.46.0.0");Q0=makeQuery(id+"F13.boolean.opBoolean","SPLIT",FACE,{"disambiguationData":[TD([makeQuery(id+"F3.opExtrude","SWEPT_FACE",FACE,{"disambiguationData":[OSD([subQ29])]})])],"derivedFrom":makeQuery(id+"F7.opExtrude","CAP_FACE",FACE,{"disambiguationData":[OSD([sQuery(id+"F6.wireOp",EDGE,"E5.bottom"),subQ33,subQ34,sQuery(id+"F6.wireOp",EDGE,"E5.right"),subQ26,subQ25,subQ24,subQ23,subQ22,subQ27,subQ35,subQ36,subQ37,subQ38,subQ39,subQ30,subQ40,subQ32,subQ41,subQ42,subQ43,subQ44,subQ21,subQ20,subQ19,subQ18,subQ17,subQ16,subQ15,subQ14,subQ13,subQ12,subQ11,subQ10,subQ9,subQ8,subQ7,subQ6,subQ28,subQ5,subQ31,subQ4,subQ3,subQ2,subQ1,subQ0,subQ45,subQ46,subQ47,subQ48,subQ49,sQuery(id+"F6.wireOp",EDGE,"E7.47.0.0"),sQuery(id+"F6.wireOp",EDGE,"E7.48.0.0"),sQuery(id+"F6.wireOp",EDGE,"E7.49.0.0"),sQuery(id+"F6.wireOp",EDGE,"E7.50.0.0"),sQuery(id+"F6.wireOp",EDGE,"E7.51.0.0"),sQuery(id+"F6.wireOp",EDGE,"E7.52.0.0"),sQuery(id+"F6.wireOp",EDGE,"E7.53.0.0")])],"isStart":true})});}
            var sketch = newSketch(context, id + "F17", { "sketchPlane" : qUnion([Q0])});
            skLineSegment(sketch, "E20.bottom", {"start": v(-190.5, -502.92) * mm, "end": v(196.85, -502.92) * mm});
            skLineSegment(sketch, "E20.top", {"start": v(-190.5, -248.92) * mm, "end": v(196.85, -248.92) * mm});
            skLineSegment(sketch, "E20.left", {"start": v(-190.5, -502.92) * mm, "end": v(-190.5, -248.92) * mm});
            skLineSegment(sketch, "E20.right", {"start": v(196.85, -502.92) * mm, "end": v(196.85, -248.92) * mm});
            skSolve(sketch);
        }
        {
            var Q0;
            Q0 = qSketchRegion(id + "F17", true);
            extrude(context, id + "F18", {"entities" : qUnion([Q0]), "depth" : 12.7 * mm, "offsetDistance" : 25.4 * mm});
        }
    });
